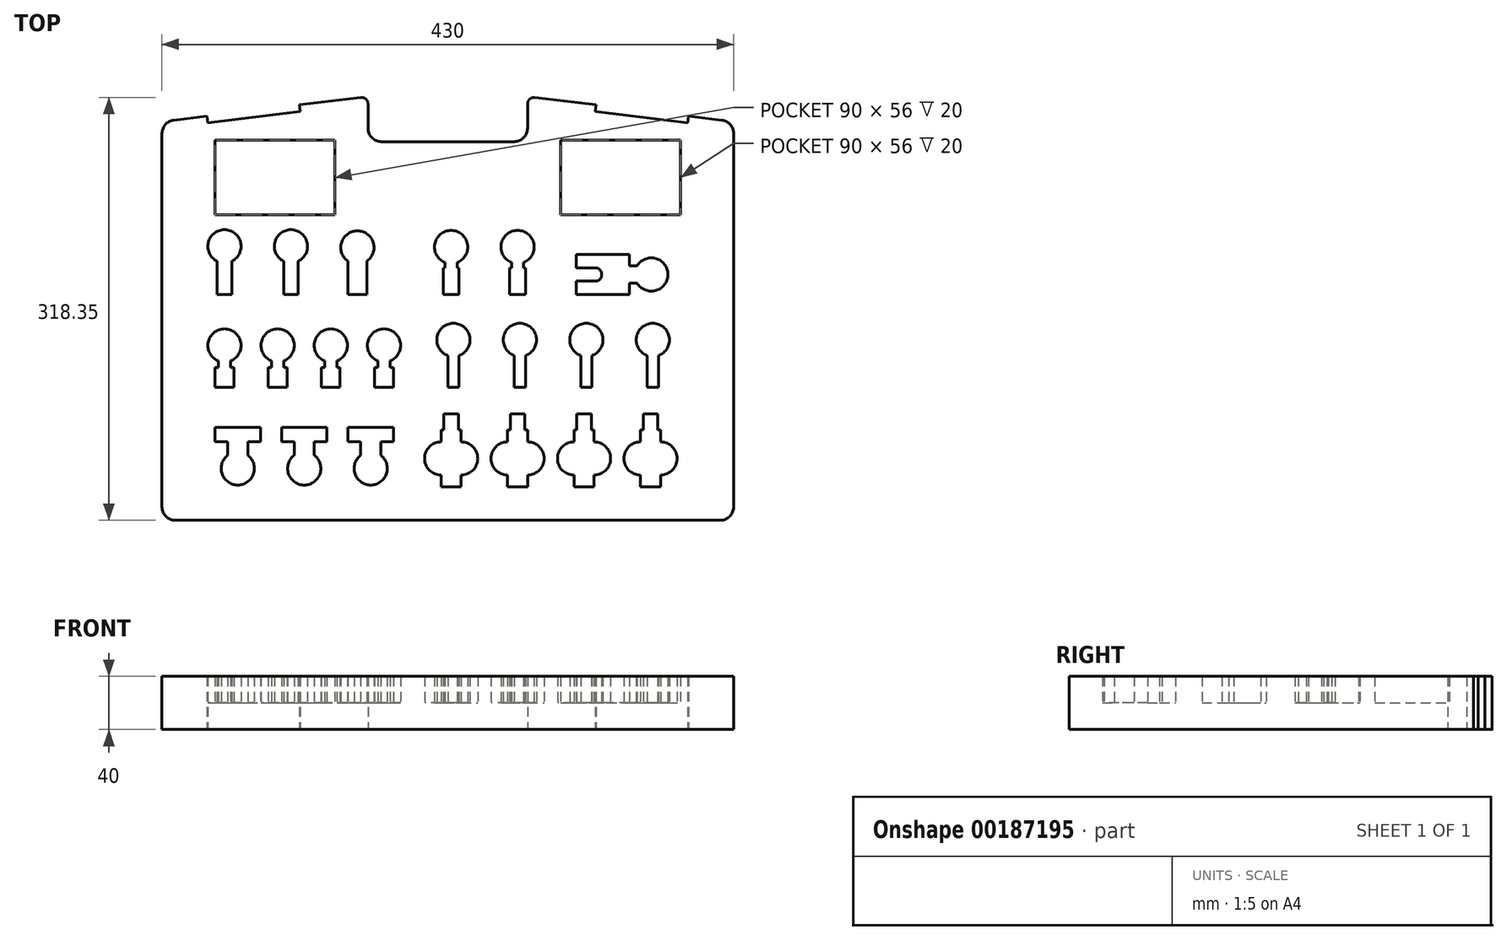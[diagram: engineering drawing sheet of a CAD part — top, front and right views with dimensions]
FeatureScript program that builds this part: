
annotation { "Feature Type Name" : "Feature", "Feature Type Description" : "" }
export const myFeature = defineFeature(function(context is Context, id is Id, definition is map)
    precondition{}
    {
        {
            var Q0;
            Q0=qCreatedBy(makeId("Top.planeOp"),FACE);
            var sketch = newSketch(context, id + "F0", { "sketchPlane" : qUnion([Q0])});
            skLineSegment(sketch, "E0.bottom", {"start": v(10, 0) * mm, "end": v(420, 0) * mm});
            skLineSegment(sketch, "E1.top", {"start": v(165, 285) * mm, "end": v(265, 285) * mm});
            skLineSegment(sketch, "E1.left", {"start": v(155, 313.35) * mm, "end": v(155, 295) * mm});
            skLineSegment(sketch, "E1.right", {"start": v(275, 313.35) * mm, "end": v(275, 295) * mm});
            skLineSegment(sketch, "E2", {"start": v(0, 10) * mm, "end": v(0, 291.15) * mm});
            skLineSegment(sketch, "E3", {"start": v(430, 10) * mm, "end": v(430, 291.15) * mm});
            skLineSegment(sketch, "E4", {"start": v(33.9, 304.16) * mm, "end": v(34.51, 299.2) * mm});
            skLineSegment(sketch, "E5", {"start": v(34.51, 299.2) * mm, "end": v(104, 307.71) * mm});
            skLineSegment(sketch, "E6", {"start": v(104, 307.71) * mm, "end": v(103.39, 312.67) * mm});
            skLineSegment(sketch, "E7", {"start": v(326.61, 312.67) * mm, "end": v(326, 307.71) * mm});
            skLineSegment(sketch, "E8", {"start": v(326, 307.71) * mm, "end": v(395.49, 299.2) * mm});
            skLineSegment(sketch, "E9", {"start": v(395.49, 299.2) * mm, "end": v(396.1, 304.16) * mm});
            skLineSegment(sketch, "E10", {"start": v(396.1, 304.16) * mm, "end": v(421.22, 301.08) * mm});
            skLineSegment(sketch, "E11", {"start": v(326.61, 312.67) * mm, "end": v(280.6, 318.31) * mm});
            skLineSegment(sketch, "E12", {"start": v(103.39, 312.67) * mm, "end": v(149.4, 318.31) * mm});
            skLineSegment(sketch, "E13", {"start": v(8.78, 301.08) * mm, "end": v(33.9, 304.16) * mm});
            skPoint(sketch, "E14.visualSharp", {"position": v(155, 285) * mm});
            skArc(sketch, "E14.filletArc", {"start": v(155, 295) * mm, "mid": v(157.93, 287.93) * mm, "end": v(165, 285) * mm});
            skPoint(sketch, "E15.visualSharp", {"position": v(275, 285) * mm});
            skArc(sketch, "E15.filletArc", {"start": v(265, 285) * mm, "mid": v(272.07, 287.93) * mm, "end": v(275, 295) * mm});
            skPoint(sketch, "E16.visualSharp", {"position": v(430, 300) * mm});
            skArc(sketch, "E16.filletArc", {"start": v(430, 291.15) * mm, "mid": v(427.49, 297.78) * mm, "end": v(421.22, 301.08) * mm});
            skPoint(sketch, "E17.visualSharp", {"position": v(0, 300) * mm});
            skArc(sketch, "E17.filletArc", {"start": v(8.78, 301.08) * mm, "mid": v(2.51, 297.78) * mm, "end": v(0, 291.15) * mm});
            skPoint(sketch, "E18.visualSharp", {"position": v(0, 0) * mm});
            skArc(sketch, "E18.filletArc", {"start": v(0, 10) * mm, "mid": v(2.93, 2.93) * mm, "end": v(10, 0) * mm});
            skPoint(sketch, "E19.visualSharp", {"position": v(430, 0) * mm});
            skArc(sketch, "E19.filletArc", {"start": v(420, 0) * mm, "mid": v(427.07, 2.93) * mm, "end": v(430, 10) * mm});
            skPoint(sketch, "E20.visualSharp", {"position": v(155, 319) * mm});
            skArc(sketch, "E20.filletArc", {"start": v(155, 313.35) * mm, "mid": v(153.31, 317.1) * mm, "end": v(149.4, 318.31) * mm});
            skPoint(sketch, "E21.visualSharp", {"position": v(275, 319) * mm});
            skArc(sketch, "E21.filletArc", {"start": v(280.6, 318.31) * mm, "mid": v(276.69, 317.1) * mm, "end": v(275, 313.35) * mm});
            skLineSegment(sketch, "E22.bottom", {"start": v(40, 59) * mm, "end": v(49.5, 59) * mm});
            skLineSegment(sketch, "E22.top", {"start": v(40, 70) * mm, "end": v(74, 70) * mm});
            skLineSegment(sketch, "E22.left", {"start": v(40, 59) * mm, "end": v(40, 70) * mm});
            skLineSegment(sketch, "E22.right", {"start": v(74, 59) * mm, "end": v(74, 70) * mm});
            skLineSegment(sketch, "E23.left", {"start": v(49.5, 59) * mm, "end": v(49.5, 49) * mm});
            skLineSegment(sketch, "E23.right", {"start": v(64.5, 59) * mm, "end": v(64.5, 49) * mm});
            skLineSegment(sketch, "E24", {"start": v(57, 70) * mm, "end": v(57, 26.5) * mm, "construction": true});
            skLineSegment(sketch, "E25.trimOffspring", {"start": v(64.5, 59) * mm, "end": v(74, 59) * mm});
            skArc(sketch, "E26", {"start": v(49.5, 49) * mm, "mid": v(57, 26.5) * mm, "end": v(64.5, 49) * mm});
            skLineSegment(sketch, "E27.1.0.0", {"start": v(90, 59) * mm, "end": v(99.5, 59) * mm});
            skLineSegment(sketch, "E27.1.0.1", {"start": v(90, 70) * mm, "end": v(124, 70) * mm});
            skLineSegment(sketch, "E27.1.0.2", {"start": v(90, 59) * mm, "end": v(90, 70) * mm});
            skLineSegment(sketch, "E27.1.0.3", {"start": v(124, 59) * mm, "end": v(124, 70) * mm});
            skLineSegment(sketch, "E27.1.0.4", {"start": v(99.5, 59) * mm, "end": v(99.5, 49) * mm});
            skLineSegment(sketch, "E27.1.0.5", {"start": v(114.5, 59) * mm, "end": v(114.5, 49) * mm});
            skLineSegment(sketch, "E27.1.0.6", {"start": v(107, 70) * mm, "end": v(107, 26.5) * mm, "construction": true});
            skLineSegment(sketch, "E27.1.0.7", {"start": v(114.5, 59) * mm, "end": v(124, 59) * mm});
            skArc(sketch, "E27.1.0.8", {"start": v(99.5, 49) * mm, "mid": v(107, 26.5) * mm, "end": v(114.5, 49) * mm});
            skLineSegment(sketch, "E27.2.0.0", {"start": v(140, 59) * mm, "end": v(149.5, 59) * mm});
            skLineSegment(sketch, "E27.2.0.1", {"start": v(140, 70) * mm, "end": v(174, 70) * mm});
            skLineSegment(sketch, "E27.2.0.2", {"start": v(140, 59) * mm, "end": v(140, 70) * mm});
            skLineSegment(sketch, "E27.2.0.3", {"start": v(174, 59) * mm, "end": v(174, 70) * mm});
            skLineSegment(sketch, "E27.2.0.4", {"start": v(149.5, 59) * mm, "end": v(149.5, 49) * mm});
            skLineSegment(sketch, "E27.2.0.5", {"start": v(164.5, 59) * mm, "end": v(164.5, 49) * mm});
            skLineSegment(sketch, "E27.2.0.6", {"start": v(157, 70) * mm, "end": v(157, 26.5) * mm, "construction": true});
            skLineSegment(sketch, "E27.2.0.7", {"start": v(164.5, 59) * mm, "end": v(174, 59) * mm});
            skArc(sketch, "E27.2.0.8", {"start": v(149.5, 49) * mm, "mid": v(157, 26.5) * mm, "end": v(164.5, 49) * mm});
            skLineSegment(sketch, "E27.direction1", {"start": v(57, 26.5) * mm, "end": v(107, 26.5) * mm, "construction": true});
            skLineSegment(sketch, "E28", {"start": v(351.5, 170) * mm, "end": v(311.5, 170) * mm});
            skLineSegment(sketch, "E29", {"start": v(311.5, 170) * mm, "end": v(311.5, 180) * mm});
            skLineSegment(sketch, "E30", {"start": v(311.5, 180) * mm, "end": v(325.8, 180) * mm});
            skLineSegment(sketch, "E31", {"start": v(325.8, 190) * mm, "end": v(311.5, 190) * mm});
            skLineSegment(sketch, "E32", {"start": v(311.5, 190) * mm, "end": v(311.5, 200) * mm});
            skLineSegment(sketch, "E33", {"start": v(311.5, 200) * mm, "end": v(351.5, 200) * mm});
            skLineSegment(sketch, "E34", {"start": v(351.5, 200) * mm, "end": v(351.5, 191.5) * mm});
            skLineSegment(sketch, "E35", {"start": v(351.5, 191.5) * mm, "end": v(357.5, 191.5) * mm});
            skLineSegment(sketch, "E36", {"start": v(357.5, 178.5) * mm, "end": v(351.5, 178.5) * mm});
            skLineSegment(sketch, "E37", {"start": v(351.5, 178.5) * mm, "end": v(351.5, 170) * mm});
            skLineSegment(sketch, "E38", {"start": v(380.68, 185) * mm, "end": v(330.8, 185) * mm, "construction": true});
            skArc(sketch, "E39", {"start": v(325.8, 180) * mm, "mid": v(330.8, 185) * mm, "end": v(325.8, 190) * mm});
            skArc(sketch, "E40", {"start": v(357.5, 178.5) * mm, "mid": v(380.68, 185) * mm, "end": v(357.5, 191.5) * mm});
            skLineSegment(sketch, "E41.bottom", {"start": v(223.5, 100) * mm, "end": v(223.5, 124) * mm});
            skLineSegment(sketch, "E41.top", {"start": v(215, 100) * mm, "end": v(215, 124) * mm});
            skLineSegment(sketch, "E41.left", {"start": v(223.5, 100) * mm, "end": v(215, 100) * mm});
            skArc(sketch, "E42", {"start": v(223.5, 124) * mm, "mid": v(219.25, 148.26) * mm, "end": v(215, 124) * mm});
            skLineSegment(sketch, "E43.1.0.0", {"start": v(273.5, 100) * mm, "end": v(265, 100) * mm});
            skArc(sketch, "E43.1.0.1", {"start": v(273.5, 124) * mm, "mid": v(269.25, 148.26) * mm, "end": v(265, 124) * mm});
            skLineSegment(sketch, "E43.1.0.2", {"start": v(265, 100) * mm, "end": v(265, 124) * mm});
            skLineSegment(sketch, "E43.1.0.3", {"start": v(273.5, 100) * mm, "end": v(273.5, 124) * mm});
            skLineSegment(sketch, "E43.2.0.0", {"start": v(323.5, 100) * mm, "end": v(315, 100) * mm});
            skArc(sketch, "E43.2.0.1", {"start": v(323.5, 124) * mm, "mid": v(319.25, 148.26) * mm, "end": v(315, 124) * mm});
            skLineSegment(sketch, "E43.2.0.2", {"start": v(315, 100) * mm, "end": v(315, 124) * mm});
            skLineSegment(sketch, "E43.2.0.3", {"start": v(323.5, 100) * mm, "end": v(323.5, 124) * mm});
            skLineSegment(sketch, "E43.3.0.0", {"start": v(373.5, 100) * mm, "end": v(365, 100) * mm});
            skArc(sketch, "E43.3.0.1", {"start": v(373.5, 124) * mm, "mid": v(369.25, 148.26) * mm, "end": v(365, 124) * mm});
            skLineSegment(sketch, "E43.3.0.2", {"start": v(365, 100) * mm, "end": v(365, 124) * mm});
            skLineSegment(sketch, "E43.3.0.3", {"start": v(373.5, 100) * mm, "end": v(373.5, 124) * mm});
            skLineSegment(sketch, "E43.direction1", {"start": v(215, 100) * mm, "end": v(265, 100) * mm, "construction": true});
            skLineSegment(sketch, "E44.bottom", {"start": v(40, 100) * mm, "end": v(54, 100) * mm});
            skLineSegment(sketch, "E44.top", {"start": v(40, 115) * mm, "end": v(42.25, 115) * mm});
            skLineSegment(sketch, "E44.left", {"start": v(40, 100) * mm, "end": v(40, 115) * mm});
            skLineSegment(sketch, "E44.right", {"start": v(54, 100) * mm, "end": v(54, 115) * mm});
            skLineSegment(sketch, "E45.left", {"start": v(42.25, 115) * mm, "end": v(42.25, 120) * mm});
            skLineSegment(sketch, "E45.right", {"start": v(51.75, 115) * mm, "end": v(51.75, 120) * mm});
            skLineSegment(sketch, "E46", {"start": v(47, 144.06) * mm, "end": v(47, 100) * mm, "construction": true});
            skArc(sketch, "E47", {"start": v(51.75, 120) * mm, "mid": v(47, 144.06) * mm, "end": v(42.25, 120) * mm});
            skLineSegment(sketch, "E48.trimOffspring", {"start": v(51.75, 115) * mm, "end": v(54, 115) * mm});
            skLineSegment(sketch, "E49.1.0.0", {"start": v(80, 100) * mm, "end": v(94, 100) * mm});
            skLineSegment(sketch, "E49.1.0.1", {"start": v(80, 115) * mm, "end": v(82.25, 115) * mm});
            skLineSegment(sketch, "E49.1.0.2", {"start": v(80, 100) * mm, "end": v(80, 115) * mm});
            skLineSegment(sketch, "E49.1.0.3", {"start": v(94, 100) * mm, "end": v(94, 115) * mm});
            skLineSegment(sketch, "E49.1.0.4", {"start": v(82.25, 115) * mm, "end": v(82.25, 120) * mm});
            skLineSegment(sketch, "E49.1.0.5", {"start": v(91.75, 115) * mm, "end": v(91.75, 120) * mm});
            skLineSegment(sketch, "E49.1.0.6", {"start": v(87, 144.06) * mm, "end": v(87, 100) * mm, "construction": true});
            skArc(sketch, "E49.1.0.7", {"start": v(91.75, 120) * mm, "mid": v(87, 144.06) * mm, "end": v(82.25, 120) * mm});
            skLineSegment(sketch, "E49.1.0.8", {"start": v(91.75, 115) * mm, "end": v(94, 115) * mm});
            skLineSegment(sketch, "E49.direction1", {"start": v(40, 100) * mm, "end": v(80, 100) * mm, "construction": true});
            skLineSegment(sketch, "E50.0.2.0", {"start": v(120, 100) * mm, "end": v(134, 100) * mm});
            skLineSegment(sketch, "E50.3.2.0", {"start": v(120, 115) * mm, "end": v(122.25, 115) * mm});
            skLineSegment(sketch, "E50.6.2.0", {"start": v(120, 100) * mm, "end": v(120, 115) * mm});
            skLineSegment(sketch, "E50.9.2.0", {"start": v(134, 100) * mm, "end": v(134, 115) * mm});
            skLineSegment(sketch, "E50.12.2.0", {"start": v(122.25, 115) * mm, "end": v(122.25, 120) * mm});
            skLineSegment(sketch, "E50.15.2.0", {"start": v(131.75, 115) * mm, "end": v(131.75, 120) * mm});
            skLineSegment(sketch, "E50.18.2.0", {"start": v(127, 144.06) * mm, "end": v(127, 100) * mm, "construction": true});
            skArc(sketch, "E50.21.2.0", {"start": v(131.75, 120) * mm, "mid": v(127, 144.06) * mm, "end": v(122.25, 120) * mm});
            skLineSegment(sketch, "E50.25.2.0", {"start": v(131.75, 115) * mm, "end": v(134, 115) * mm});
            skLineSegment(sketch, "E50.0.3.0", {"start": v(160, 100) * mm, "end": v(174, 100) * mm});
            skLineSegment(sketch, "E50.3.3.0", {"start": v(160, 115) * mm, "end": v(162.25, 115) * mm});
            skLineSegment(sketch, "E50.6.3.0", {"start": v(160, 100) * mm, "end": v(160, 115) * mm});
            skLineSegment(sketch, "E50.9.3.0", {"start": v(174, 100) * mm, "end": v(174, 115) * mm});
            skLineSegment(sketch, "E50.12.3.0", {"start": v(162.25, 115) * mm, "end": v(162.25, 120) * mm});
            skLineSegment(sketch, "E50.15.3.0", {"start": v(171.75, 115) * mm, "end": v(171.75, 120) * mm});
            skLineSegment(sketch, "E50.18.3.0", {"start": v(167, 144.06) * mm, "end": v(167, 100) * mm, "construction": true});
            skArc(sketch, "E50.21.3.0", {"start": v(171.75, 120) * mm, "mid": v(167, 144.06) * mm, "end": v(162.25, 120) * mm});
            skLineSegment(sketch, "E50.25.3.0", {"start": v(171.75, 115) * mm, "end": v(174, 115) * mm});
            skLineSegment(sketch, "E51.bottom", {"start": v(41.5, 170) * mm, "end": v(52.5, 170) * mm});
            skLineSegment(sketch, "E51.left", {"start": v(41.5, 170) * mm, "end": v(41.5, 195) * mm});
            skLineSegment(sketch, "E51.right", {"start": v(52.5, 170) * mm, "end": v(52.5, 195) * mm});
            skArc(sketch, "E52", {"start": v(52.5, 195) * mm, "mid": v(47, 218.72) * mm, "end": v(41.5, 195) * mm});
            skLineSegment(sketch, "E53", {"start": v(47, 218.72) * mm, "end": v(47, 170) * mm, "construction": true});
            skLineSegment(sketch, "E54.1.0.0", {"start": v(91.5, 170) * mm, "end": v(102.5, 170) * mm});
            skLineSegment(sketch, "E54.1.0.1", {"start": v(91.5, 170) * mm, "end": v(91.5, 195) * mm});
            skLineSegment(sketch, "E54.1.0.2", {"start": v(102.5, 170) * mm, "end": v(102.5, 195) * mm});
            skArc(sketch, "E54.1.0.3", {"start": v(102.5, 195) * mm, "mid": v(97, 218.72) * mm, "end": v(91.5, 195) * mm});
            skLineSegment(sketch, "E54.1.0.4", {"start": v(97, 218.72) * mm, "end": v(97, 170) * mm, "construction": true});
            skLineSegment(sketch, "E54.direction1", {"start": v(41.5, 170) * mm, "end": v(91.5, 170) * mm, "construction": true});
            skLineSegment(sketch, "E55.bottom", {"start": v(140, 170) * mm, "end": v(154, 170) * mm});
            skLineSegment(sketch, "E55.left", {"start": v(140, 170) * mm, "end": v(140, 195) * mm});
            skLineSegment(sketch, "E55.right", {"start": v(154, 170) * mm, "end": v(154, 195) * mm});
            skLineSegment(sketch, "E56", {"start": v(147, 217.86) * mm, "end": v(147, 170) * mm, "construction": true});
            skArc(sketch, "E57", {"start": v(154, 195) * mm, "mid": v(147, 217.86) * mm, "end": v(140, 195) * mm});
            skLineSegment(sketch, "E58.bottom", {"start": v(211.5, 170) * mm, "end": v(223.5, 170) * mm});
            skLineSegment(sketch, "E58.top", {"start": v(211.5, 190) * mm, "end": v(213, 190) * mm});
            skLineSegment(sketch, "E58.left", {"start": v(211.5, 170) * mm, "end": v(211.5, 190) * mm});
            skLineSegment(sketch, "E58.right", {"start": v(223.5, 170) * mm, "end": v(223.5, 190) * mm});
            skLineSegment(sketch, "E59.left", {"start": v(213, 190) * mm, "end": v(213, 194) * mm});
            skLineSegment(sketch, "E59.right", {"start": v(222, 190) * mm, "end": v(222, 194) * mm});
            skLineSegment(sketch, "E60", {"start": v(217.5, 218.16) * mm, "end": v(217.5, 170) * mm, "construction": true});
            skArc(sketch, "E61", {"start": v(222, 194) * mm, "mid": v(217.5, 218.16) * mm, "end": v(213, 194) * mm});
            skLineSegment(sketch, "E62.trimOffspring", {"start": v(222, 190) * mm, "end": v(223.5, 190) * mm});
            skLineSegment(sketch, "E63.1.0.0", {"start": v(261.5, 170) * mm, "end": v(273.5, 170) * mm});
            skLineSegment(sketch, "E63.1.0.1", {"start": v(261.5, 190) * mm, "end": v(263, 190) * mm});
            skLineSegment(sketch, "E63.1.0.2", {"start": v(261.5, 170) * mm, "end": v(261.5, 190) * mm});
            skLineSegment(sketch, "E63.1.0.3", {"start": v(273.5, 170) * mm, "end": v(273.5, 190) * mm});
            skLineSegment(sketch, "E63.1.0.4", {"start": v(263, 190) * mm, "end": v(263, 194) * mm});
            skLineSegment(sketch, "E63.1.0.5", {"start": v(272, 190) * mm, "end": v(272, 194) * mm});
            skLineSegment(sketch, "E63.1.0.6", {"start": v(267.5, 218.16) * mm, "end": v(267.5, 170) * mm, "construction": true});
            skArc(sketch, "E63.1.0.7", {"start": v(272, 194) * mm, "mid": v(267.5, 218.16) * mm, "end": v(263, 194) * mm});
            skLineSegment(sketch, "E63.1.0.8", {"start": v(272, 190) * mm, "end": v(273.5, 190) * mm});
            skLineSegment(sketch, "E63.direction1", {"start": v(211.5, 170) * mm, "end": v(261.5, 170) * mm, "construction": true});
            skLineSegment(sketch, "E64.bottom", {"start": v(210, 25) * mm, "end": v(210, 34) * mm});
            skLineSegment(sketch, "E64.top", {"start": v(225, 25) * mm, "end": v(225, 34) * mm});
            skLineSegment(sketch, "E64.left", {"start": v(210, 25) * mm, "end": v(225, 25) * mm});
            skLineSegment(sketch, "E64.right", {"start": v(210, 68) * mm, "end": v(212, 68) * mm});
            skLineSegment(sketch, "E65", {"start": v(217.5, 25) * mm, "end": v(217.5, 80) * mm, "construction": true});
            skLineSegment(sketch, "E66.bottom", {"start": v(212, 68) * mm, "end": v(212, 80) * mm});
            skLineSegment(sketch, "E66.top", {"start": v(223, 68) * mm, "end": v(223, 80) * mm});
            skLineSegment(sketch, "E66.right", {"start": v(212, 80) * mm, "end": v(223, 80) * mm});
            skLineSegment(sketch, "E67.trimOffspring", {"start": v(223, 68) * mm, "end": v(225, 68) * mm});
            skArc(sketch, "E68", {"start": v(210, 59) * mm, "mid": v(197.5, 46.5) * mm, "end": v(210, 34) * mm});
            skArc(sketch, "E69", {"start": v(225, 34) * mm, "mid": v(237.5, 46.5) * mm, "end": v(225, 59) * mm});
            skLineSegment(sketch, "E70.trimOffspring", {"start": v(225, 59) * mm, "end": v(225, 68) * mm});
            skLineSegment(sketch, "E71.trimOffspring", {"start": v(210, 59) * mm, "end": v(210, 68) * mm});
            skLineSegment(sketch, "E72.1.0.0", {"start": v(275, 25) * mm, "end": v(275, 34) * mm});
            skArc(sketch, "E72.1.0.1", {"start": v(260, 59) * mm, "mid": v(247.5, 46.5) * mm, "end": v(260, 34) * mm});
            skLineSegment(sketch, "E72.1.0.2", {"start": v(267.5, 25) * mm, "end": v(267.5, 80) * mm, "construction": true});
            skLineSegment(sketch, "E72.1.0.3", {"start": v(260, 25) * mm, "end": v(275, 25) * mm});
            skLineSegment(sketch, "E72.1.0.4", {"start": v(260, 25) * mm, "end": v(260, 34) * mm});
            skLineSegment(sketch, "E72.1.0.5", {"start": v(273, 68) * mm, "end": v(273, 80) * mm});
            skArc(sketch, "E72.1.0.6", {"start": v(275, 34) * mm, "mid": v(287.5, 46.5) * mm, "end": v(275, 59) * mm});
            skLineSegment(sketch, "E72.1.0.7", {"start": v(260, 59) * mm, "end": v(260, 68) * mm});
            skLineSegment(sketch, "E72.1.0.8", {"start": v(262, 68) * mm, "end": v(262, 80) * mm});
            skLineSegment(sketch, "E72.1.0.9", {"start": v(275, 59) * mm, "end": v(275, 68) * mm});
            skLineSegment(sketch, "E72.1.0.10", {"start": v(262, 80) * mm, "end": v(273, 80) * mm});
            skLineSegment(sketch, "E72.1.0.11", {"start": v(260, 68) * mm, "end": v(262, 68) * mm});
            skLineSegment(sketch, "E72.1.0.12", {"start": v(273, 68) * mm, "end": v(275, 68) * mm});
            skLineSegment(sketch, "E72.2.0.0", {"start": v(325, 25) * mm, "end": v(325, 34) * mm});
            skArc(sketch, "E72.2.0.1", {"start": v(310, 59) * mm, "mid": v(297.5, 46.5) * mm, "end": v(310, 34) * mm});
            skLineSegment(sketch, "E72.2.0.2", {"start": v(317.5, 25) * mm, "end": v(317.5, 80) * mm, "construction": true});
            skLineSegment(sketch, "E72.2.0.3", {"start": v(310, 25) * mm, "end": v(325, 25) * mm});
            skLineSegment(sketch, "E72.2.0.4", {"start": v(310, 25) * mm, "end": v(310, 34) * mm});
            skLineSegment(sketch, "E72.2.0.5", {"start": v(323, 68) * mm, "end": v(323, 80) * mm});
            skArc(sketch, "E72.2.0.6", {"start": v(325, 34) * mm, "mid": v(337.5, 46.5) * mm, "end": v(325, 59) * mm});
            skLineSegment(sketch, "E72.2.0.7", {"start": v(310, 59) * mm, "end": v(310, 68) * mm});
            skLineSegment(sketch, "E72.2.0.8", {"start": v(312, 68) * mm, "end": v(312, 80) * mm});
            skLineSegment(sketch, "E72.2.0.9", {"start": v(325, 59) * mm, "end": v(325, 68) * mm});
            skLineSegment(sketch, "E72.2.0.10", {"start": v(312, 80) * mm, "end": v(323, 80) * mm});
            skLineSegment(sketch, "E72.2.0.11", {"start": v(310, 68) * mm, "end": v(312, 68) * mm});
            skLineSegment(sketch, "E72.2.0.12", {"start": v(323, 68) * mm, "end": v(325, 68) * mm});
            skLineSegment(sketch, "E72.3.0.0", {"start": v(375, 25) * mm, "end": v(375, 34) * mm});
            skArc(sketch, "E72.3.0.1", {"start": v(360, 59) * mm, "mid": v(347.5, 46.5) * mm, "end": v(360, 34) * mm});
            skLineSegment(sketch, "E72.3.0.2", {"start": v(367.5, 25) * mm, "end": v(367.5, 80) * mm, "construction": true});
            skLineSegment(sketch, "E72.3.0.3", {"start": v(360, 25) * mm, "end": v(375, 25) * mm});
            skLineSegment(sketch, "E72.3.0.4", {"start": v(360, 25) * mm, "end": v(360, 34) * mm});
            skLineSegment(sketch, "E72.3.0.5", {"start": v(373, 68) * mm, "end": v(373, 80) * mm});
            skArc(sketch, "E72.3.0.6", {"start": v(375, 34) * mm, "mid": v(387.5, 46.5) * mm, "end": v(375, 59) * mm});
            skLineSegment(sketch, "E72.3.0.7", {"start": v(360, 59) * mm, "end": v(360, 68) * mm});
            skLineSegment(sketch, "E72.3.0.8", {"start": v(362, 68) * mm, "end": v(362, 80) * mm});
            skLineSegment(sketch, "E72.3.0.9", {"start": v(375, 59) * mm, "end": v(375, 68) * mm});
            skLineSegment(sketch, "E72.3.0.10", {"start": v(362, 80) * mm, "end": v(373, 80) * mm});
            skLineSegment(sketch, "E72.3.0.11", {"start": v(360, 68) * mm, "end": v(362, 68) * mm});
            skLineSegment(sketch, "E72.3.0.12", {"start": v(373, 68) * mm, "end": v(375, 68) * mm});
            skLineSegment(sketch, "E72.direction1", {"start": v(210, 25) * mm, "end": v(260, 25) * mm, "construction": true});
            skLineSegment(sketch, "E73.bottom", {"start": v(40, 230) * mm, "end": v(130, 230) * mm});
            skLineSegment(sketch, "E73.top", {"start": v(40, 286) * mm, "end": v(130, 286) * mm});
            skLineSegment(sketch, "E73.left", {"start": v(40, 230) * mm, "end": v(40, 286) * mm});
            skLineSegment(sketch, "E73.right", {"start": v(130, 230) * mm, "end": v(130, 286) * mm});
            skLineSegment(sketch, "E74.1.0.0", {"start": v(300, 230) * mm, "end": v(390, 230) * mm});
            skLineSegment(sketch, "E74.1.0.1", {"start": v(390, 230) * mm, "end": v(390, 286) * mm});
            skLineSegment(sketch, "E74.1.0.2", {"start": v(300, 286) * mm, "end": v(390, 286) * mm});
            skLineSegment(sketch, "E74.1.0.3", {"start": v(300, 230) * mm, "end": v(300, 286) * mm});
            skLineSegment(sketch, "E74.direction1", {"start": v(40, 230) * mm, "end": v(300, 230) * mm, "construction": true});
            skSolve(sketch);
        }
        {
            var Q0;
            Q0 = qSketchRegion(id + "F0", true);
            extrude(context, id + "F1", {"entities" : qUnion([Q0]), "depth" : 20 * mm});
        }
        {
            var Q0;
            Q0=makeQuery(id+"F0.imprint","IMPRINT",FACE,{"disambiguationData":[TD([[makeQuery(id+"F0.imprint","IMPRINT",EDGE,{"derivedFrom":sQuery(id+"F0.wireOp",EDGE,"E0.bottom")}),1.0]])]});
            var Q1;
            Q1=makeQuery(id+"F0.imprint","IMPRINT",FACE,{"disambiguationData":[TD([[makeQuery(id+"F0.imprint","IMPRINT",EDGE,{"derivedFrom":sQuery(id+"F0.wireOp",EDGE,"E73.bottom")}),1.0]])]});
            var Q2;
            Q2=makeQuery(id+"F0.imprint","IMPRINT",FACE,{"disambiguationData":[TD([[makeQuery(id+"F0.imprint","IMPRINT",EDGE,{"derivedFrom":sQuery(id+"F0.wireOp",EDGE,"E74.1.0.0")}),1.0]])]});
            var Q3;
            Q3=makeQuery(id+"F0.imprint","IMPRINT",FACE,{"disambiguationData":[TD([[makeQuery(id+"F0.imprint","IMPRINT",EDGE,{"derivedFrom":sQuery(id+"F0.wireOp",EDGE,"E28")}),-1.0]])]});
            var Q4;
            Q4=makeQuery(id+"F0.imprint","IMPRINT",FACE,{"disambiguationData":[TD([[makeQuery(id+"F0.imprint","IMPRINT",EDGE,{"derivedFrom":sQuery(id+"F0.wireOp",EDGE,"E63.1.0.0")}),1.0]])]});
            var Q5;
            Q5=makeQuery(id+"F0.imprint","IMPRINT",FACE,{"disambiguationData":[TD([[makeQuery(id+"F0.imprint","IMPRINT",EDGE,{"derivedFrom":sQuery(id+"F0.wireOp",EDGE,"E58.bottom")}),1.0]])]});
            var Q6;
            Q6=makeQuery(id+"F0.imprint","IMPRINT",FACE,{"disambiguationData":[TD([[makeQuery(id+"F0.imprint","IMPRINT",EDGE,{"derivedFrom":sQuery(id+"F0.wireOp",EDGE,"E55.bottom")}),1.0]])]});
            var Q7;
            Q7=makeQuery(id+"F0.imprint","IMPRINT",FACE,{"disambiguationData":[TD([[makeQuery(id+"F0.imprint","IMPRINT",EDGE,{"derivedFrom":sQuery(id+"F0.wireOp",EDGE,"E54.1.0.0")}),1.0]])]});
            var Q8;
            Q8=makeQuery(id+"F0.imprint","IMPRINT",FACE,{"disambiguationData":[TD([[makeQuery(id+"F0.imprint","IMPRINT",EDGE,{"derivedFrom":sQuery(id+"F0.wireOp",EDGE,"E51.bottom")}),1.0]])]});
            var Q9;
            Q9=makeQuery(id+"F0.imprint","IMPRINT",FACE,{"disambiguationData":[TD([[makeQuery(id+"F0.imprint","IMPRINT",EDGE,{"derivedFrom":sQuery(id+"F0.wireOp",EDGE,"E44.bottom")}),1.0]])]});
            var Q10;
            Q10=makeQuery(id+"F0.imprint","IMPRINT",FACE,{"disambiguationData":[TD([[makeQuery(id+"F0.imprint","IMPRINT",EDGE,{"derivedFrom":sQuery(id+"F0.wireOp",EDGE,"E49.1.0.0")}),1.0]])]});
            var Q11;
            Q11=makeQuery(id+"F0.imprint","IMPRINT",FACE,{"disambiguationData":[TD([[makeQuery(id+"F0.imprint","IMPRINT",EDGE,{"derivedFrom":sQuery(id+"F0.wireOp",EDGE,"E50.0.2.0")}),1.0]])]});
            var Q12;
            Q12=makeQuery(id+"F0.imprint","IMPRINT",FACE,{"disambiguationData":[TD([[makeQuery(id+"F0.imprint","IMPRINT",EDGE,{"derivedFrom":sQuery(id+"F0.wireOp",EDGE,"E50.0.3.0")}),1.0]])]});
            var Q13;
            Q13=makeQuery(id+"F0.imprint","IMPRINT",FACE,{"disambiguationData":[TD([[makeQuery(id+"F0.imprint","IMPRINT",EDGE,{"derivedFrom":sQuery(id+"F0.wireOp",EDGE,"E41.bottom")}),1.0]])]});
            var Q14;
            Q14=makeQuery(id+"F0.imprint","IMPRINT",FACE,{"disambiguationData":[TD([[makeQuery(id+"F0.imprint","IMPRINT",EDGE,{"derivedFrom":sQuery(id+"F0.wireOp",EDGE,"E43.1.0.0")}),-1.0]])]});
            var Q15;
            Q15=makeQuery(id+"F0.imprint","IMPRINT",FACE,{"disambiguationData":[TD([[makeQuery(id+"F0.imprint","IMPRINT",EDGE,{"derivedFrom":sQuery(id+"F0.wireOp",EDGE,"E43.2.0.0")}),-1.0]])]});
            var Q16;
            Q16=makeQuery(id+"F0.imprint","IMPRINT",FACE,{"disambiguationData":[TD([[makeQuery(id+"F0.imprint","IMPRINT",EDGE,{"derivedFrom":sQuery(id+"F0.wireOp",EDGE,"E43.3.0.0")}),-1.0]])]});
            var Q17;
            Q17=makeQuery(id+"F0.imprint","IMPRINT",FACE,{"disambiguationData":[TD([[makeQuery(id+"F0.imprint","IMPRINT",EDGE,{"derivedFrom":sQuery(id+"F0.wireOp",EDGE,"E72.3.0.0")}),1.0]])]});
            var Q18;
            Q18=makeQuery(id+"F0.imprint","IMPRINT",FACE,{"disambiguationData":[TD([[makeQuery(id+"F0.imprint","IMPRINT",EDGE,{"derivedFrom":sQuery(id+"F0.wireOp",EDGE,"E72.2.0.0")}),1.0]])]});
            var Q19;
            Q19=makeQuery(id+"F0.imprint","IMPRINT",FACE,{"disambiguationData":[TD([[makeQuery(id+"F0.imprint","IMPRINT",EDGE,{"derivedFrom":sQuery(id+"F0.wireOp",EDGE,"E72.1.0.0")}),1.0]])]});
            var Q20;
            Q20=makeQuery(id+"F0.imprint","IMPRINT",FACE,{"disambiguationData":[TD([[makeQuery(id+"F0.imprint","IMPRINT",EDGE,{"derivedFrom":sQuery(id+"F0.wireOp",EDGE,"E64.bottom")}),-1.0]])]});
            var Q21;
            Q21=makeQuery(id+"F0.imprint","IMPRINT",FACE,{"disambiguationData":[TD([[makeQuery(id+"F0.imprint","IMPRINT",EDGE,{"derivedFrom":sQuery(id+"F0.wireOp",EDGE,"E27.2.0.0")}),1.0]])]});
            var Q22;
            Q22=makeQuery(id+"F0.imprint","IMPRINT",FACE,{"disambiguationData":[TD([[makeQuery(id+"F0.imprint","IMPRINT",EDGE,{"derivedFrom":sQuery(id+"F0.wireOp",EDGE,"E27.1.0.0")}),1.0]])]});
            var Q23;
            Q23=makeQuery(id+"F0.imprint","IMPRINT",FACE,{"disambiguationData":[TD([[makeQuery(id+"F0.imprint","IMPRINT",EDGE,{"derivedFrom":sQuery(id+"F0.wireOp",EDGE,"E22.bottom")}),1.0]])]});
            var Q24;
            Q24=makeQuery(id+"F0.imprint","IMPRINT",FACE,{"disambiguationData":[TD([[makeQuery(id+"F0.imprint","IMPRINT",EDGE,{"derivedFrom":sQuery(id+"F0.wireOp",EDGE,"45c8c606-81b5-4f72-ab21-82beb55337fc")}),1.0]])]});
            extrude(context, id + "F2", {"entities" : qUnion([Q0, Q1, Q2, Q3, Q4, Q5, Q6, Q7, Q8, Q9, Q10, Q11, Q12, Q13, Q14, Q15, Q16, Q17, Q18, Q19, Q20, Q21, Q22, Q23, Q24]), "operationType" : NewBodyOperationType.ADD, "oppositeDirection" : true, "depth" : 20 * mm});
        }
    });
